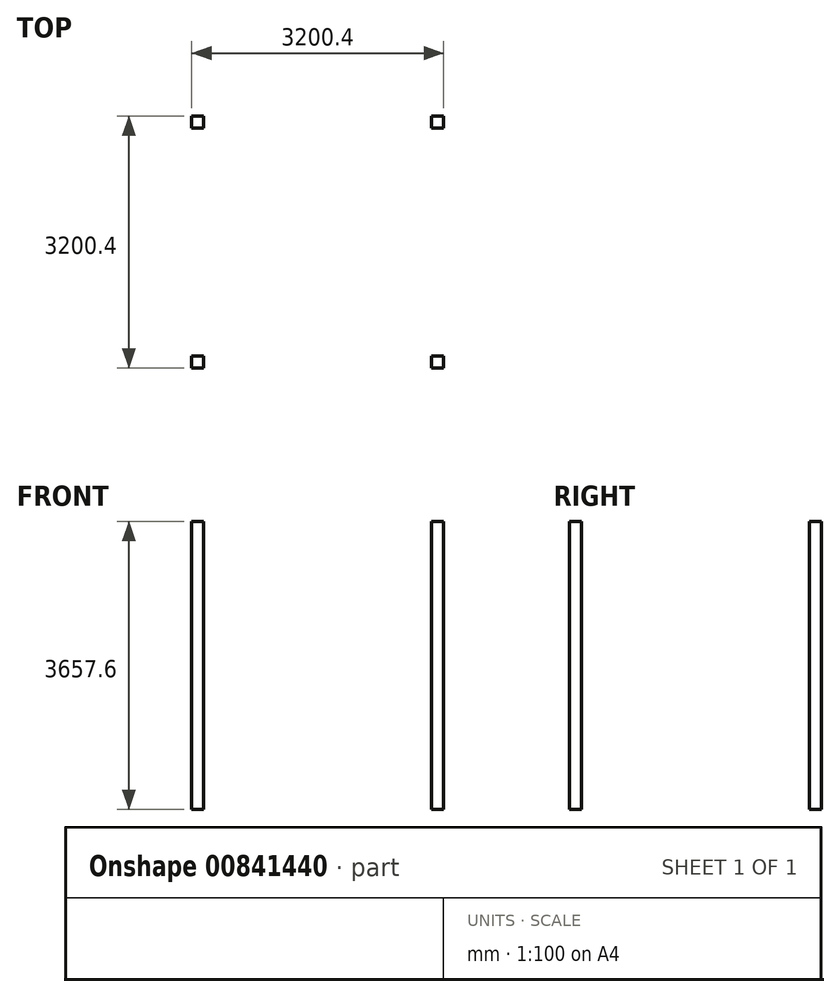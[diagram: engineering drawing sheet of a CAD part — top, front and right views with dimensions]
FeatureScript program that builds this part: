
annotation { "Feature Type Name" : "Feature", "Feature Type Description" : "" }
export const myFeature = defineFeature(function(context is Context, id is Id, definition is map)
    precondition{}
    {
        {
            var Q0;
            Q0=qCreatedBy(makeId("Top.planeOp"),FACE);
            var sketch = newSketch(context, id + "F0", { "sketchPlane" : qUnion([Q0])});
            skLineSegment(sketch, "E0.bottom", {"start": v(-136.8, -146.57) * mm, "end": v(15.6, -146.57) * mm});
            skLineSegment(sketch, "E0.top", {"start": v(-136.8, 5.83) * mm, "end": v(15.6, 5.83) * mm});
            skLineSegment(sketch, "E0.left", {"start": v(-136.8, -146.57) * mm, "end": v(-136.8, 5.83) * mm});
            skLineSegment(sketch, "E0.right", {"start": v(15.6, -146.57) * mm, "end": v(15.6, 5.83) * mm});
            skLineSegment(sketch, "E1.0.1.0", {"start": v(15.6, 2901.43) * mm, "end": v(15.6, 3053.83) * mm});
            skLineSegment(sketch, "E1.0.1.1", {"start": v(-136.8, 2901.43) * mm, "end": v(-136.8, 3053.83) * mm});
            skLineSegment(sketch, "E1.0.1.2", {"start": v(-136.8, 3053.83) * mm, "end": v(15.6, 3053.83) * mm});
            skLineSegment(sketch, "E1.0.1.3", {"start": v(-136.8, 2901.43) * mm, "end": v(15.6, 2901.43) * mm});
            skLineSegment(sketch, "E1.1.0.0", {"start": v(3063.6, -146.57) * mm, "end": v(3063.6, 5.83) * mm});
            skLineSegment(sketch, "E1.1.0.1", {"start": v(2911.2, -146.57) * mm, "end": v(2911.2, 5.83) * mm});
            skLineSegment(sketch, "E1.1.0.2", {"start": v(2911.2, 5.83) * mm, "end": v(3063.6, 5.83) * mm});
            skLineSegment(sketch, "E1.1.0.3", {"start": v(2911.2, -146.57) * mm, "end": v(3063.6, -146.57) * mm});
            skLineSegment(sketch, "E1.1.1.0", {"start": v(3063.6, 2901.43) * mm, "end": v(3063.6, 3053.83) * mm});
            skLineSegment(sketch, "E1.1.1.1", {"start": v(2911.2, 2901.43) * mm, "end": v(2911.2, 3053.83) * mm});
            skLineSegment(sketch, "E1.1.1.2", {"start": v(2911.2, 3053.83) * mm, "end": v(3063.6, 3053.83) * mm});
            skLineSegment(sketch, "E1.1.1.3", {"start": v(2911.2, 2901.43) * mm, "end": v(3063.6, 2901.43) * mm});
            skLineSegment(sketch, "E1.direction1", {"start": v(-136.8, -146.57) * mm, "end": v(2911.2, -146.57) * mm, "construction": true});
            skLineSegment(sketch, "E1.direction2", {"start": v(-136.8, -146.57) * mm, "end": v(-136.8, 2901.43) * mm, "construction": true});
            skSolve(sketch);
        }
        {
            var Q0;
            Q0=makeQuery(id+"F0.imprint","IMPRINT",FACE,{"disambiguationData":[TD([[makeQuery(id+"F0.imprint","IMPRINT",EDGE,{"derivedFrom":sQuery(id+"F0.wireOp",EDGE,"E0.bottom")}),1.0]])]});
            var Q1;
            Q1=makeQuery(id+"F0.imprint","IMPRINT",FACE,{"disambiguationData":[TD([[makeQuery(id+"F0.imprint","IMPRINT",EDGE,{"derivedFrom":sQuery(id+"F0.wireOp",EDGE,"E1.1.0.0")}),1.0]])]});
            var Q2;
            Q2=makeQuery(id+"F0.imprint","IMPRINT",FACE,{"disambiguationData":[TD([[makeQuery(id+"F0.imprint","IMPRINT",EDGE,{"derivedFrom":sQuery(id+"F0.wireOp",EDGE,"E1.0.1.0")}),1.0]])]});
            var Q3;
            Q3=makeQuery(id+"F0.imprint","IMPRINT",FACE,{"disambiguationData":[TD([[makeQuery(id+"F0.imprint","IMPRINT",EDGE,{"derivedFrom":sQuery(id+"F0.wireOp",EDGE,"E1.1.1.0")}),1.0]])]});
            extrude(context, id + "F1", {"entities" : qUnion([Q0, Q1, Q2, Q3]), "depth" : 3657.6 * mm, "offsetDistance" : 25.4 * mm});
        }
    });
